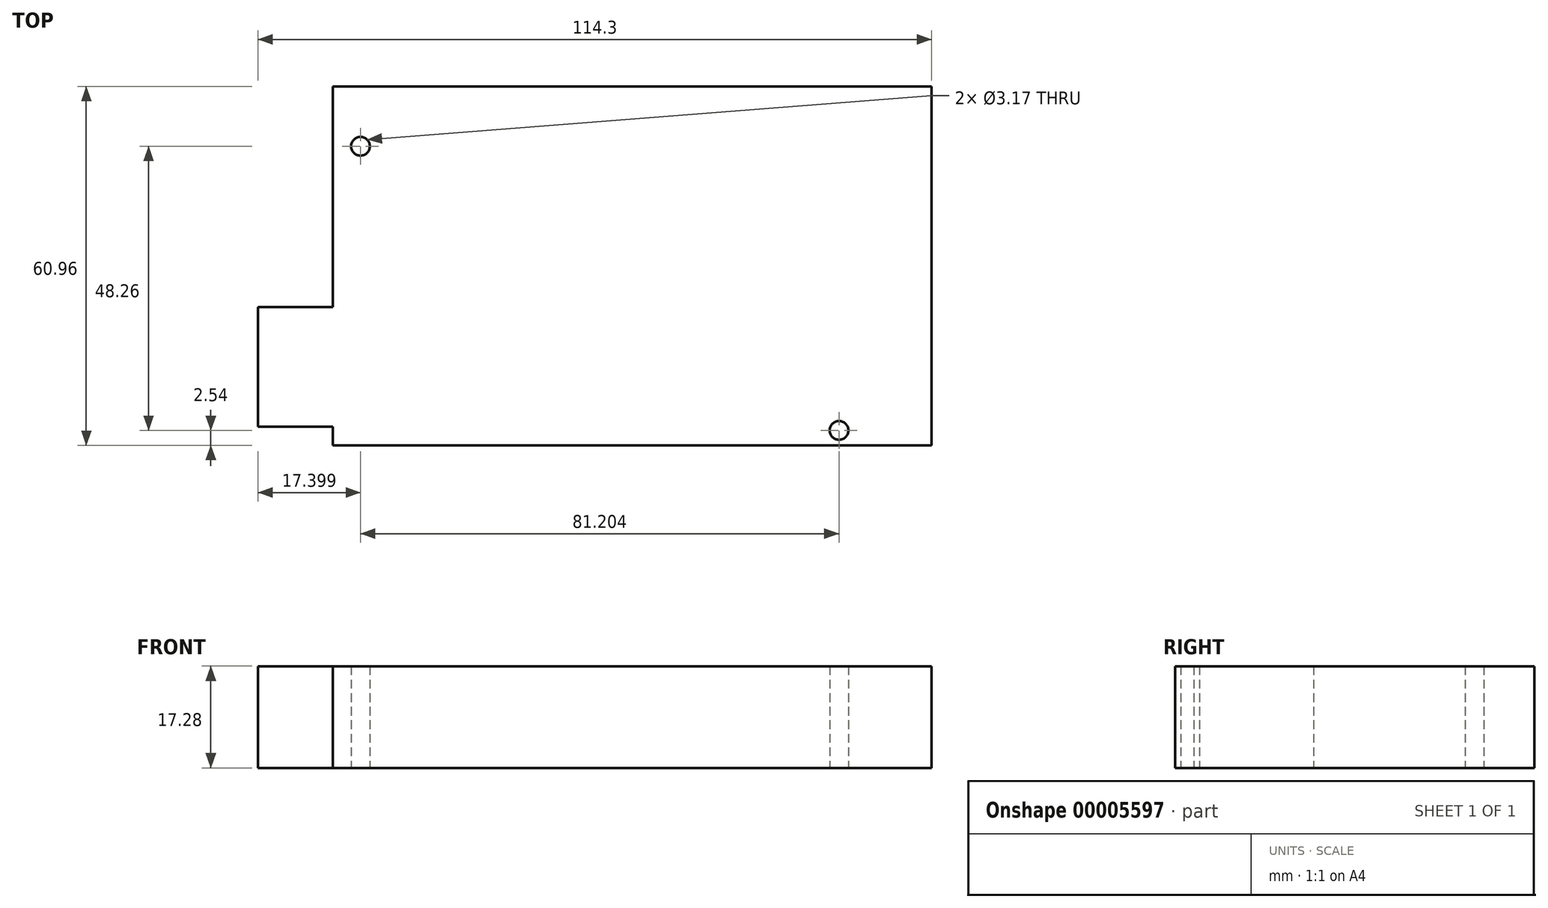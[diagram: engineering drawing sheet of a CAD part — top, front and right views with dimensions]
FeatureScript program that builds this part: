
annotation { "Feature Type Name" : "Feature", "Feature Type Description" : "" }
export const myFeature = defineFeature(function(context is Context, id is Id, definition is map)
    precondition{}
    {
        {
            var Q0;
            Q0=qCreatedBy(makeId("Top.planeOp"),FACE);
            var sketch = newSketch(context, id + "F0", { "sketchPlane" : qUnion([Q0])});
            skLineSegment(sketch, "E0.bottom", {"start": v(-50.8, 30.48) * mm, "end": v(50.8, 30.48) * mm, "construction": true});
            skLineSegment(sketch, "E0.top", {"start": v(-50.8, -30.48) * mm, "end": v(50.8, -30.48) * mm, "construction": true});
            skLineSegment(sketch, "E0.left", {"start": v(-50.8, 30.48) * mm, "end": v(-50.8, -30.48) * mm, "construction": true});
            skLineSegment(sketch, "E0.right", {"start": v(50.8, 30.48) * mm, "end": v(50.8, -30.48) * mm, "construction": true});
            skCircle(sketch, "E1", {"center": v(35.1, -27.94) * mm, "radius": 1.59 * mm});
            skCircle(sketch, "E2", {"center": v(-46.1, 20.32) * mm, "radius": 1.59 * mm});
            skLineSegment(sketch, "E3.bottom", {"start": v(-63.5, -6.98) * mm, "end": v(-44.45, -6.98) * mm});
            skLineSegment(sketch, "E3.top", {"start": v(-63.5, -27.3) * mm, "end": v(-44.45, -27.3) * mm});
            skLineSegment(sketch, "E3.left", {"start": v(-63.5, -6.99) * mm, "end": v(-63.5, -27.3) * mm});
            skLineSegment(sketch, "E3.right", {"start": v(-44.45, -6.98) * mm, "end": v(-44.45, -27.3) * mm});
            skLineSegment(sketch, "E4.bottom", {"start": v(-50.8, 30.48) * mm, "end": v(50.8, 30.48) * mm});
            skLineSegment(sketch, "E4.top", {"start": v(-50.8, -30.48) * mm, "end": v(50.8, -30.48) * mm});
            skLineSegment(sketch, "E4.left", {"start": v(-50.8, 30.48) * mm, "end": v(-50.8, -30.48) * mm});
            skLineSegment(sketch, "E4.right", {"start": v(50.8, 30.48) * mm, "end": v(50.8, -30.48) * mm});
            skSolve(sketch);
        }
        {
            var Q0;
            {var subQ5=sQuery(id+"F0.wireOp",EDGE,"E3.left");Q0=makeQuery(id+"F0.imprint","IMPRINT",FACE,{"disambiguationData":[TD([[makeQuery(id+"F0.imprint","IMPRINT",EDGE,{"derivedFrom":subQ5}),1.0]])]});}
            var Q1;
            {var subQ5=sQuery(id+"F0.wireOp",EDGE,"E3.right");Q1=makeQuery(id+"F0.imprint","IMPRINT",FACE,{"disambiguationData":[TD([[makeQuery(id+"F0.imprint","IMPRINT",EDGE,{"derivedFrom":subQ5}),-1.0]])]});}
            var Q2;
            Q2=makeQuery(id+"F0.imprint","IMPRINT",FACE,{"disambiguationData":[TD([[makeQuery(id+"F0.imprint","IMPRINT",EDGE,{"derivedFrom":sQuery(id+"F0.wireOp",EDGE,"E1")}),-1.0]])]});
            extrude(context, id + "F1", {"entities" : qUnion([Q0, Q1, Q2]), "depth" : 17.27 * mm, "symmetric" : true});
        }
    });
